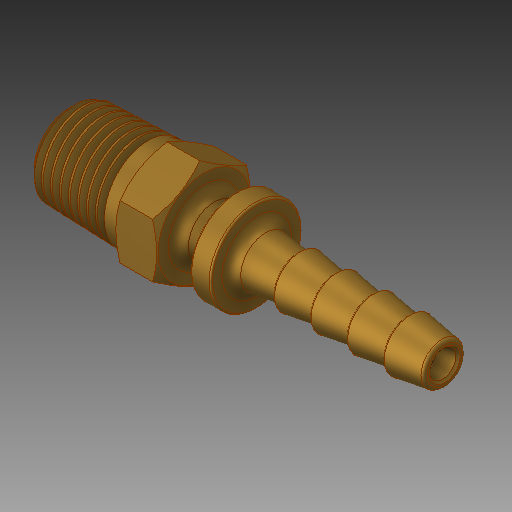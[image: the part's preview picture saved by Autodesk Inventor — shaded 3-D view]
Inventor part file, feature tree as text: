
AUTODESK INVENTOR PART (.ipt)
format: ipt  version: 2018 (Build 220112000, 112)  size: 777,728 bytes
history: native  units: in
note: dims shown in document units (in); Inventor stores cm internally (conversion verified against a paired STEP export)
features: extrude x1
ambient origin geometry x8: Origin, YZ Plane, XZ Plane, XY Plane, X Axis, Y Axis, Z Axis, Center Point
bodies: Solid1 (feature_tree)
feature tree (1):
  extrude  "Extrude1"  [1 undecoded]
note: 1 required parameter value undecoded (feature->parameter linkage not recoverable at this tier; creation-order binding heuristic only, values carry confidence <= 0.55)
